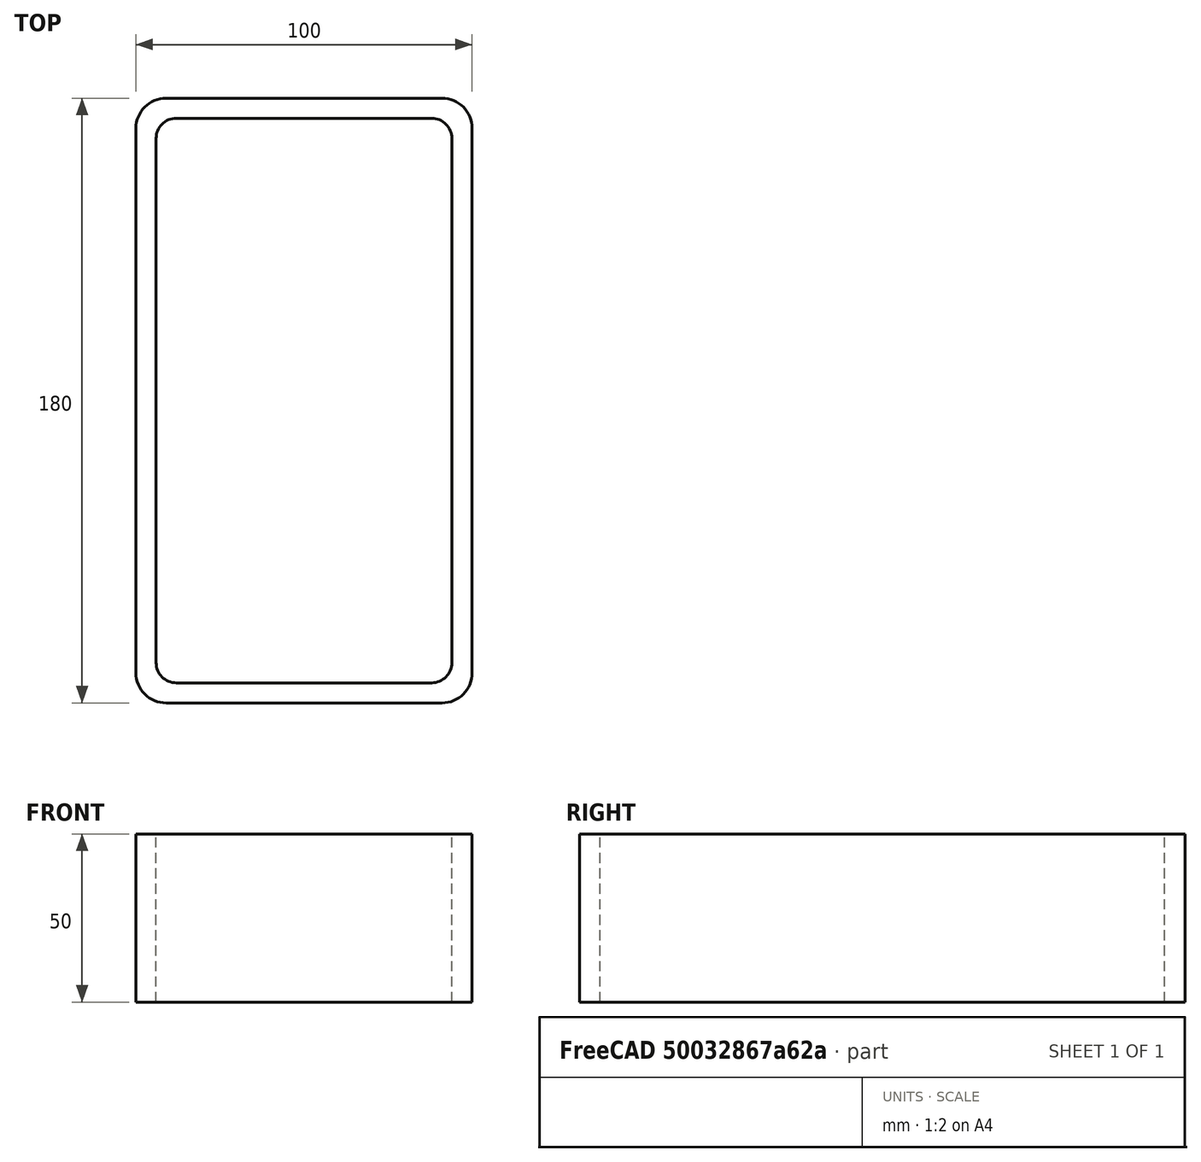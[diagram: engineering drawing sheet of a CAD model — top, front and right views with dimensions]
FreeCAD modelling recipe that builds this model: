
FCSTD DOCUMENT  (FreeCAD 0.15R4671 (Git))
Label: Rectangular hollow section 180x100x6 EN10219 S235JRH
License: All rights reserved
LicenseURL: http://en.wikipedia.org/wiki/All_rights_reserved
objects: Sketcher::SketchObject×1, Part::Extrusion×1
note: 2 computed .brp shape members not serialized (recipe doc carries the construction recipe); baked Part::Feature solids carry a one-line shape summary decoded from their .brp

FEATURE [Sketcher::SketchObject] Sketch
  sketch-geometry (16):
    g0: LineSegment StartX=-38 StartY=84 StartZ=0 EndX=38 EndY=84 EndZ=0
    g1: LineSegment StartX=44 StartY=78 StartZ=0 EndX=44 EndY=-78 EndZ=0
    g2: LineSegment StartX=38 StartY=-84 StartZ=0 EndX=-38 EndY=-84 EndZ=0
    g3: LineSegment StartX=-44 StartY=-78 StartZ=0 EndX=-44 EndY=78 EndZ=0
    g4: LineSegment StartX=-41 StartY=90 StartZ=0 EndX=41 EndY=90 EndZ=0
    g5: LineSegment StartX=50 StartY=81 StartZ=0 EndX=50 EndY=-81 EndZ=0
    g6: LineSegment StartX=41 StartY=-90 StartZ=0 EndX=-41 EndY=-90 EndZ=0
    g7: LineSegment StartX=-50 StartY=-81 StartZ=0 EndX=-50 EndY=81 EndZ=0
    g8: ArcOfCircle CenterX=-38 CenterY=78 CenterZ=0 NormalX=0 NormalY=0 NormalZ=1 Radius=6 StartAngle=1.5708 EndAngle=3.14159
    g9: ArcOfCircle CenterX=38 CenterY=78 CenterZ=0 NormalX=0 NormalY=0 NormalZ=1 Radius=6 StartAngle=0 EndAngle=1.5708
    g10: ArcOfCircle CenterX=38 CenterY=-78 CenterZ=0 NormalX=0 NormalY=0 NormalZ=1 Radius=6 StartAngle=4.71239 EndAngle=6.28319
    g11: ArcOfCircle CenterX=-38 CenterY=-78 CenterZ=0 NormalX=0 NormalY=0 NormalZ=1 Radius=6 StartAngle=3.14159 EndAngle=4.71239
    g12: ArcOfCircle CenterX=41 CenterY=81 CenterZ=0 NormalX=0 NormalY=0 NormalZ=1 Radius=9 StartAngle=0 EndAngle=1.5708
    g13: ArcOfCircle CenterX=41 CenterY=-81 CenterZ=0 NormalX=0 NormalY=0 NormalZ=1 Radius=9 StartAngle=4.71239 EndAngle=6.28319
    g14: ArcOfCircle CenterX=-41 CenterY=-81 CenterZ=0 NormalX=0 NormalY=0 NormalZ=1 Radius=9 StartAngle=3.14159 EndAngle=4.71239
    g15: ArcOfCircle CenterX=-41 CenterY=81 CenterZ=0 NormalX=0 NormalY=0 NormalZ=1 Radius=9 StartAngle=1.5708 EndAngle=3.14159
  constraints (36):
    c: Horizontal(g2)
    c: Vertical(g3)
    c: Horizontal(g6)
    c: Vertical(g7)
    c: Tangent(g3,g8) = 1.5708
    c: Tangent(g0,g8) = 1.5708
    c: Tangent(g0,g9) = 1.5708
    c: Tangent(g1,g9) = 1.5708
    c: Tangent(g1,g10) = 1.5708
    c: Tangent(g2,g10) = 1.5708
    c: Tangent(g2,g11) = 1.5708
    c: Tangent(g3,g11) = 1.5708
    c: Tangent(g4,g12) = 1.5708
    c: Tangent(g5,g12) = 1.5708
    c: Tangent(g5,g13) = 1.5708
    c: Tangent(g6,g13) = 1.5708
    c: Tangent(g6,g14) = 1.5708
    c: Tangent(g7,g14) = 1.5708
    c: Tangent(g7,g15) = 1.5708
    c: Tangent(g4,g15) = 1.5708
    c: Equal(g9,g8)
    c: Equal(g9,g11)
    c: Equal(g9,g10)
    c: Equal(g12,g15)
    c: Equal(g12,g14)
    c: Equal(g12,g13)
    c: Symmetric(g4,g6,g-1)
    c: Symmetric(g7,g5,g-2)
    c: DistanceY(g4,g6) = -180
    c: DistanceX(g7,g5) = 100
    c: Symmetric(g3,g1,g-2)
    c: Symmetric(g0,g2,g-1)
    c: DistanceY(g0,g4) = 6
    c: DistanceX(g5,g1) = -6
    c: Radius(g9) = 6
    c: Radius(g12) = 9
FEATURE [Part::Extrusion] Extrude  label="Rectangular hollow section 180x100x6 EN10219 S235JRH"
  Base = -> Sketch
  Dir = (0,0,50)
  Solid = true
